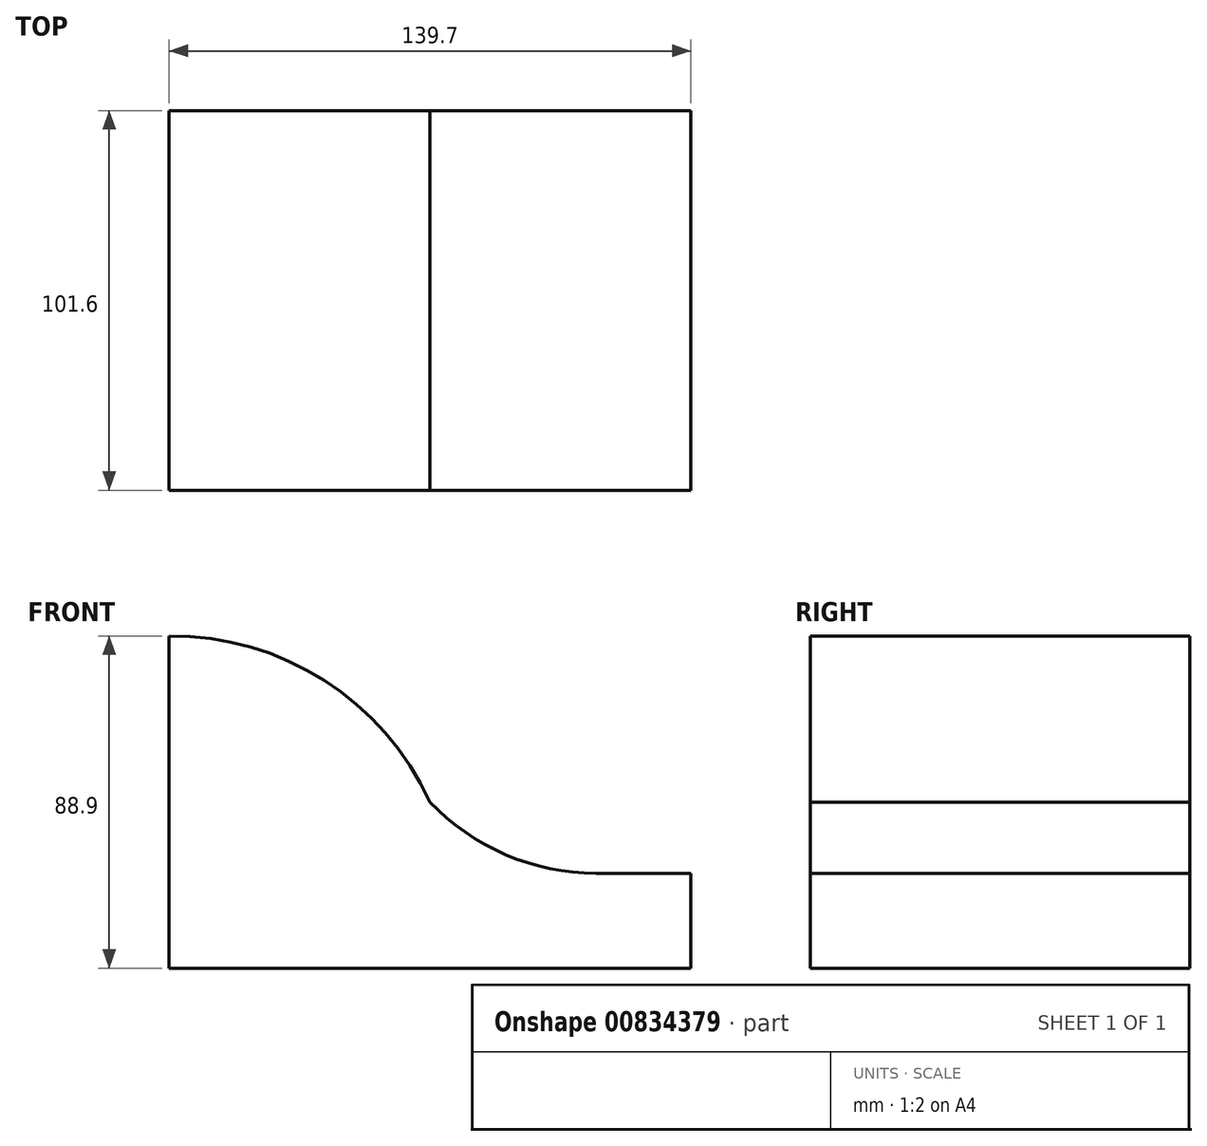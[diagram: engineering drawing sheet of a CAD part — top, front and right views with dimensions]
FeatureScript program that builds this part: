
annotation { "Feature Type Name" : "Feature", "Feature Type Description" : "" }
export const myFeature = defineFeature(function(context is Context, id is Id, definition is map)
    precondition{}
    {
        {
            var Q0;
            Q0=qCreatedBy(makeId("Front.planeOp"),FACE);
            var sketch = newSketch(context, id + "F0", { "sketchPlane" : qUnion([Q0])});
            skLineSegment(sketch, "E0", {"start": v(-69.85, 44.45) * mm, "end": v(-69.85, 0) * mm});
            skLineSegment(sketch, "E1", {"start": v(-69.85, 0) * mm, "end": v(-69.85, -44.45) * mm});
            skLineSegment(sketch, "E2", {"start": v(-69.85, -44.45) * mm, "end": v(0, -44.45) * mm});
            skLineSegment(sketch, "E3", {"start": v(0, -44.45) * mm, "end": v(69.85, -44.45) * mm});
            skArc(sketch, "E4", {"start": v(0, 0) * mm, "mid": v(-28.34, 32.57) * mm, "end": v(-69.85, 44.45) * mm});
            skLineSegment(sketch, "E5", {"start": v(69.85, -44.45) * mm, "end": v(69.85, -19.05) * mm});
            skLineSegment(sketch, "E6", {"start": v(69.85, -19.05) * mm, "end": v(44.45, -19.05) * mm});
            skArc(sketch, "E7", {"start": v(0, 0) * mm, "mid": v(20.27, -14.09) * mm, "end": v(44.45, -19.05) * mm});
            skSolve(sketch);
        }
        {
            var Q0;
            Q0 = qSketchRegion(id + "F0", true);
            extrude(context, id + "F1", {"entities" : qUnion([Q0]), "depth" : 50.8 * mm, "offsetDistance" : 25.4 * mm, "hasSecondDirection" : true, "secondDirectionOppositeDirection" : true, "secondDirectionDepth" : 50.8 * mm});
        }
    });
